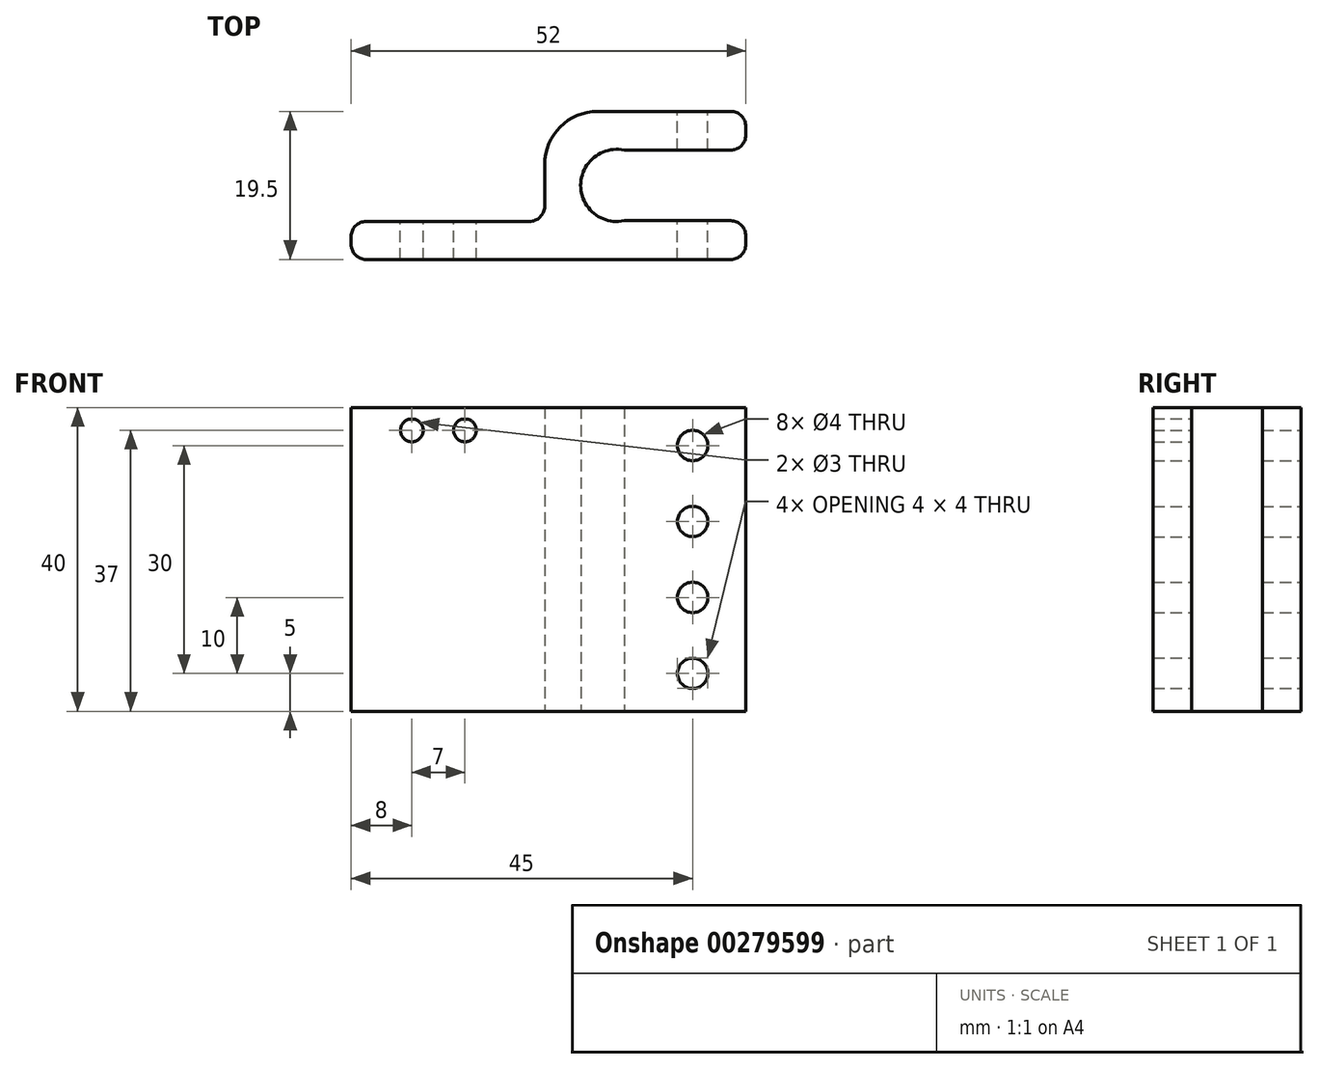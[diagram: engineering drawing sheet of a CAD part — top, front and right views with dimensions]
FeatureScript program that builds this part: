
annotation { "Feature Type Name" : "Feature", "Feature Type Description" : "" }
export const myFeature = defineFeature(function(context is Context, id is Id, definition is map)
    precondition{}
    {
        {
            var Q0;
            Q0=qCreatedBy(makeId("Top.planeOp"),FACE);
            var sketch = newSketch(context, id + "F0", { "sketchPlane" : qUnion([Q0])});
            skArc(sketch, "E0", {"start": v(0.97, 4.65) * mm, "mid": v(-4.75, 0) * mm, "end": v(0.97, -4.65) * mm});
            skLineSegment(sketch, "E1.bottom", {"start": v(-9.5, 9.75) * mm, "end": v(17, 9.75) * mm});
            skLineSegment(sketch, "E1.top", {"start": v(-9.5, -9.75) * mm, "end": v(17, -9.75) * mm});
            skLineSegment(sketch, "E1.left", {"start": v(-9.5, 9.75) * mm, "end": v(-9.5, -9.75) * mm});
            skLineSegment(sketch, "E1.right", {"start": v(17, 9.75) * mm, "end": v(17, 4.65) * mm});
            skLineSegment(sketch, "E2.bottom", {"start": v(-9.5, -9.75) * mm, "end": v(-35, -9.75) * mm});
            skLineSegment(sketch, "E2.top", {"start": v(-9.5, -4.75) * mm, "end": v(-35, -4.75) * mm});
            skLineSegment(sketch, "E2.left", {"start": v(-9.5, -9.75) * mm, "end": v(-9.5, -4.75) * mm});
            skLineSegment(sketch, "E2.right", {"start": v(-35, -9.75) * mm, "end": v(-35, -4.75) * mm});
            skLineSegment(sketch, "E3.bottom", {"start": v(17, 4.65) * mm, "end": v(0.97, 4.65) * mm});
            skLineSegment(sketch, "E3.top", {"start": v(17, -4.65) * mm, "end": v(0.97, -4.65) * mm});
            skLineSegment(sketch, "E4.trimOffspring", {"start": v(17, -4.65) * mm, "end": v(17, -9.75) * mm});
            skSolve(sketch);
        }
        {
            var Q0;
            Q0 = qSketchRegion(id + "F0", true);
            extrude(context, id + "F1", {"entities" : qUnion([Q0]), "depth" : 40 * mm});
        }
        {
            var Q0;
            Q0=qCreatedBy(makeId("Front.planeOp"),FACE);
            var sketch = newSketch(context, id + "F2", { "sketchPlane" : qUnion([Q0])});
            skCircle(sketch, "E5", {"center": v(10, 35) * mm, "radius": 2 * mm});
            skCircle(sketch, "E6", {"center": v(10, 25) * mm, "radius": 2 * mm});
            skCircle(sketch, "E7", {"center": v(10, 15) * mm, "radius": 2 * mm});
            skCircle(sketch, "E8", {"center": v(10, 5) * mm, "radius": 2 * mm});
            skCircle(sketch, "E9", {"center": v(-27, 37) * mm, "radius": 1.5 * mm});
            skCircle(sketch, "E10", {"center": v(-20, 37) * mm, "radius": 1.5 * mm});
            skSolve(sketch);
        }
        {
            var Q0;
            Q0 = qSketchRegion(id + "F2", true);
            extrude(context, id + "F3", {"entities" : qUnion([Q0]), "operationType" : NewBodyOperationType.REMOVE, "endBound" : BoundingType.SYMMETRIC, "depth" : 40 * mm});
        }
        {
            var Q0;
            Q0=makeQuery(id+"F1.opExtrude","SWEPT_EDGE",EDGE,{"disambiguationData":[OSD([sQuery(id+"F0.wireOp",EDGE,"E2.bottom"),sQuery(id+"F0.wireOp",EDGE,"E2.right")])]});
            var Q1;
            Q1=makeQuery(id+"F1.opExtrude","SWEPT_EDGE",EDGE,{"disambiguationData":[OSD([sQuery(id+"F0.wireOp",EDGE,"E2.top"),sQuery(id+"F0.wireOp",EDGE,"E2.right")])]});
            var Q2;
            Q2=makeQuery(id+"F1.opExtrude","SWEPT_EDGE",EDGE,{"disambiguationData":[OSD([sQuery(id+"F0.wireOp",EDGE,"E1.top"),sQuery(id+"F0.wireOp",EDGE,"E4.trimOffspring")])]});
            var Q3;
            Q3=makeQuery(id+"F1.opExtrude","SWEPT_EDGE",EDGE,{"disambiguationData":[OSD([sQuery(id+"F0.wireOp",EDGE,"E1.left"),sQuery(id+"F0.wireOp",EDGE,"E2.top"),sQuery(id+"F0.wireOp",EDGE,"E2.left")])]});
            var Q4;
            Q4=makeQuery(id+"F1.opExtrude","SWEPT_EDGE",EDGE,{"disambiguationData":[OSD([sQuery(id+"F0.wireOp",EDGE,"E3.top"),sQuery(id+"F0.wireOp",EDGE,"E4.trimOffspring")])]});
            var Q5;
            Q5=makeQuery(id+"F1.opExtrude","SWEPT_EDGE",EDGE,{"disambiguationData":[OSD([sQuery(id+"F0.wireOp",EDGE,"E1.right"),sQuery(id+"F0.wireOp",EDGE,"E3.bottom")])]});
            var Q6;
            Q6=makeQuery(id+"F1.opExtrude","SWEPT_EDGE",EDGE,{"disambiguationData":[OSD([sQuery(id+"F0.wireOp",EDGE,"E1.bottom"),sQuery(id+"F0.wireOp",EDGE,"E1.right")])]});
            fillet(context, id + "F4", {"entities" : qUnion([Q0, Q1, Q2, Q3, Q4, Q5, Q6]), "radius" : 2 * mm, "tangentPropagation" : true, "allowEdgeOverflow" : false});
        }
        {
            var Q0;
            Q0=makeQuery(id+"F1.opExtrude","SWEPT_EDGE",EDGE,{"disambiguationData":[OSD([sQuery(id+"F0.wireOp",EDGE,"E1.bottom"),sQuery(id+"F0.wireOp",EDGE,"E1.left")])]});
            fillet(context, id + "F5", {"entities" : qUnion([Q0]), "radius" : 7 * mm, "tangentPropagation" : true, "allowEdgeOverflow" : false});
        }
    });
